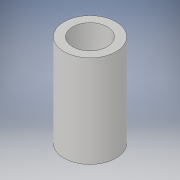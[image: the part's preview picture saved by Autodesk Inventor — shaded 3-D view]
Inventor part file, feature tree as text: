
AUTODESK INVENTOR PART (.ipt)
format: ipt  version: 2019 (Build 230136000, 136)  size: 95,744 bytes
history: native  units: mm
features: other x1, extrude x1, sketch x1
ambient origin geometry x8: Origin, YZ Plane, XZ Plane, XY Plane, X Axis, Y Axis, Z Axis, Center Point
bodies: Body1 (feature_tree)
feature tree (3):
  other  "Bryła1"
  extrude  "Wyciągnięcie proste1"  Depth=3.0mm
  sketch  "Szkic1"
